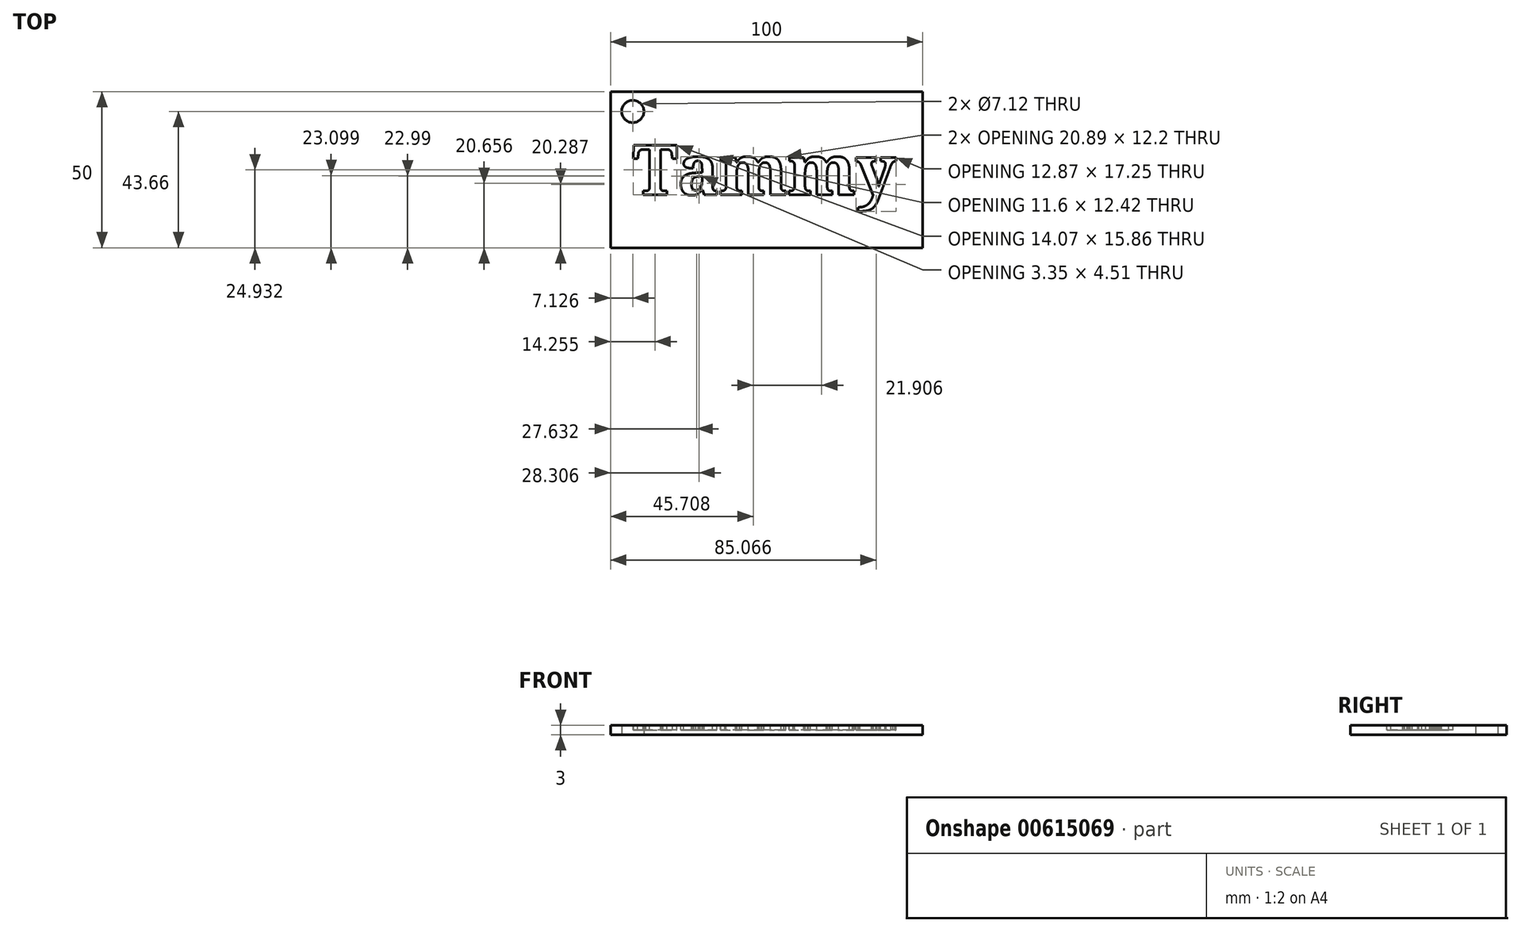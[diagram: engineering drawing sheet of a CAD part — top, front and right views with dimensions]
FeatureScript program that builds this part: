
annotation { "Feature Type Name" : "Feature", "Feature Type Description" : "" }
export const myFeature = defineFeature(function(context is Context, id is Id, definition is map)
    precondition{}
    {
        {
            var Q0;
            Q0=qCreatedBy(makeId("Top.planeOp"),FACE);
            var sketch = newSketch(context, id + "F0", { "sketchPlane" : qUnion([Q0])});
            skLineSegment(sketch, "E0.bottom", {"start": v(0, 0) * mm, "end": v(-100, 0) * mm});
            skLineSegment(sketch, "E0.top", {"start": v(0, 50) * mm, "end": v(-100, 50) * mm});
            skLineSegment(sketch, "E0.left", {"start": v(0, 0) * mm, "end": v(0, 50) * mm});
            skLineSegment(sketch, "E0.right", {"start": v(-100, 0) * mm, "end": v(-100, 50) * mm});
            skCircle(sketch, "E1", {"center": v(-92.87, 43.66) * mm, "radius": 3.56 * mm});
            skSolve(sketch);
        }
        {
            var Q0;
            Q0 = qSketchRegion(id + "F0", true);
            extrude(context, id + "F1", {"entities" : qUnion([Q0]), "depth" : 3 * mm, "offsetDistance" : 25 * mm});
        }
        {
            var Q0;
            Q0=makeQuery(id+"F1.opExtrude","CAP_FACE",FACE,{"disambiguationData":[OSD([sQuery(id+"F0.wireOp",EDGE,"E0.bottom"),sQuery(id+"F0.wireOp",EDGE,"E0.top"),sQuery(id+"F0.wireOp",EDGE,"E0.left"),sQuery(id+"F0.wireOp",EDGE,"E0.right")])],"isStart":false});
            var sketch = newSketch(context, id + "F2", { "sketchPlane" : qUnion([Q0])});
            skText(sketch, "E2", { "text": "Tammy", "fontName": "NotoSerif-Bold.ttf"});
            const initialGuessF2  = {"E2": [-0.093, 0.017, 1, 0, 0.016]};
            skSetInitialGuess(sketch, initialGuessF2);
            skSolve(sketch);
        }
        {
            var Q0;
            Q0 = qSketchRegion(id + "F2", true);
            extrude(context, id + "F3", {"entities" : qUnion([Q0]), "operationType" : NewBodyOperationType.REMOVE, "oppositeDirection" : true, "depth" : 1.5 * mm, "offsetDistance" : 25 * mm});
        }
    });
